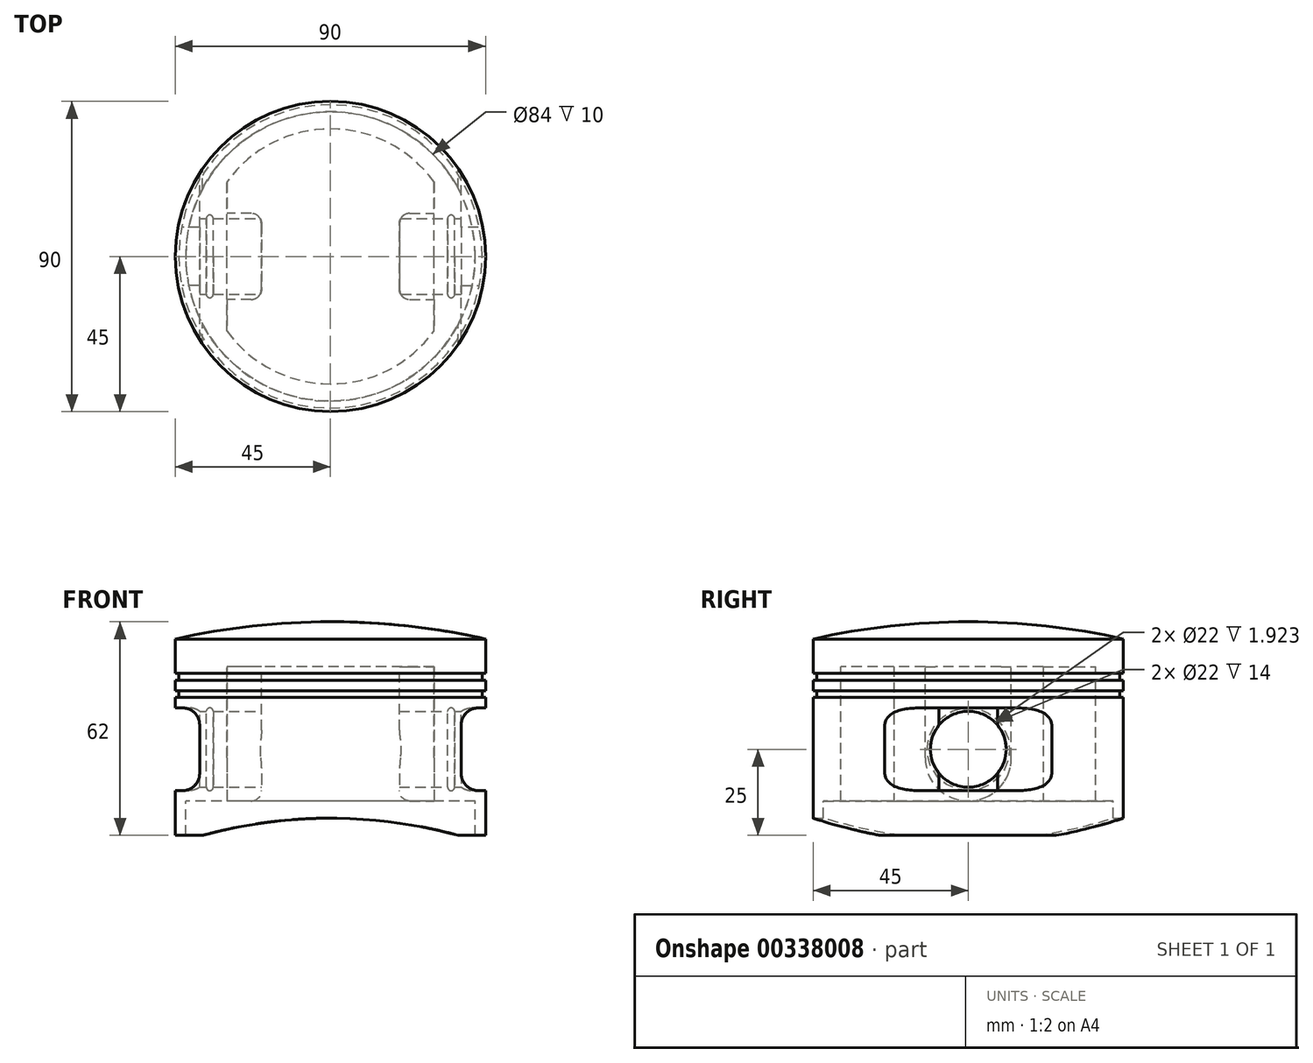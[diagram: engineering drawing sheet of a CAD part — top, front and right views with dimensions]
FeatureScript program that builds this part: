
annotation { "Feature Type Name" : "Feature", "Feature Type Description" : "" }
export const myFeature = defineFeature(function(context is Context, id is Id, definition is map)
    precondition{}
    {
        {
            var Q0;
            Q0=qCreatedBy(makeId("Front.planeOp"),FACE);
            var sketch = newSketch(context, id + "F0", { "sketchPlane" : qUnion([Q0])});
            skLineSegment(sketch, "E0", {"start": v(0, 31.06) * mm, "end": v(0, -35.72) * mm, "construction": true});
            skLineSegment(sketch, "E1", {"start": v(0, 0) * mm, "end": v(45, 0) * mm});
            skLineSegment(sketch, "E2", {"start": v(45, 0) * mm, "end": v(45, -10) * mm});
            skLineSegment(sketch, "E3", {"start": v(45, -10) * mm, "end": v(44, -10) * mm});
            skLineSegment(sketch, "E4", {"start": v(44, -10) * mm, "end": v(44, -12) * mm});
            skLineSegment(sketch, "E5", {"start": v(44, -12) * mm, "end": v(45, -12) * mm});
            skLineSegment(sketch, "E6", {"start": v(45, -12) * mm, "end": v(45, -15) * mm});
            skLineSegment(sketch, "E7", {"start": v(45, -15) * mm, "end": v(44, -15) * mm});
            skLineSegment(sketch, "E8", {"start": v(44, -15) * mm, "end": v(44, -17) * mm});
            skLineSegment(sketch, "E9", {"start": v(44, -17) * mm, "end": v(45, -17) * mm});
            skLineSegment(sketch, "E10", {"start": v(45, -17) * mm, "end": v(45, -57) * mm});
            skLineSegment(sketch, "E11", {"start": v(45, -57) * mm, "end": v(42, -57) * mm});
            skLineSegment(sketch, "E12", {"start": v(42, -57) * mm, "end": v(42, -47) * mm});
            skLineSegment(sketch, "E13", {"start": v(42, -47) * mm, "end": v(37, -47) * mm});
            skLineSegment(sketch, "E14", {"start": v(37, -47) * mm, "end": v(37, -8) * mm});
            skLineSegment(sketch, "E15", {"start": v(37, -8) * mm, "end": v(0, -8) * mm});
            skLineSegment(sketch, "E16", {"start": v(0, -8) * mm, "end": v(0, 0) * mm});
            skSolve(sketch);
        }
        {
            var Q0;
            Q0 = qSketchRegion(id + "F0", true);
            var Q1;
            Q1=sQuery(id+"F0.wireOp",EDGE,"E0");
            revolve(context, id + "F1", {"entities" : qUnion([Q0]), "axis" : qUnion([Q1]), "revolveType" : RevolveType.FULL});
        }
        {
            var Q0;
            Q0=qCreatedBy(makeId("Front.planeOp"),FACE);
            var sketch = newSketch(context, id + "F2", { "sketchPlane" : qUnion([Q0])});
            skLineSegment(sketch, "E17.bottom", {"start": v(51.92, -20) * mm, "end": v(37.92, -20) * mm});
            skLineSegment(sketch, "E17.top", {"start": v(51.92, -44) * mm, "end": v(37.92, -44) * mm});
            skLineSegment(sketch, "E17.left", {"start": v(51.92, -20) * mm, "end": v(51.92, -44) * mm});
            skLineSegment(sketch, "E17.right", {"start": v(37.92, -20) * mm, "end": v(37.92, -44) * mm});
            skPoint(sketch, "E17.middle", {"position": v(44.92, -32) * mm});
            skLineSegment(sketch, "E18.MirrorCS", {"start": v(-51.92, -20) * mm, "end": v(-37.92, -20) * mm});
            skLineSegment(sketch, "E19.MirrorCS", {"start": v(-37.92, -20) * mm, "end": v(-37.92, -44) * mm});
            skLineSegment(sketch, "E20.MirrorCS", {"start": v(-51.92, -44) * mm, "end": v(-37.92, -44) * mm});
            skLineSegment(sketch, "E21.MirrorCS", {"start": v(-51.92, -20) * mm, "end": v(-51.92, -44) * mm});
            skSolve(sketch);
        }
        {
            var Q0;
            Q0 = qSketchRegion(id + "F2", true);
            extrude(context, id + "F3", {"entities" : qUnion([Q0]), "operationType" : NewBodyOperationType.REMOVE, "depth" : 100 * mm, "symmetric" : true});
        }
        {
            var Q0;
            Q0=makeQuery(id+"F1.opRevolve","SWEPT_FACE",FACE,{"disambiguationData":[OSD([sQuery(id+"F0.wireOp",EDGE,"E13")])]});
            var sketch = newSketch(context, id + "F4", { "sketchPlane" : qUnion([Q0])});
            skLineSegment(sketch, "E22", {"start": v(0, 42) * mm, "end": v(0, -42) * mm, "construction": true});
            skLineSegment(sketch, "E23", {"start": v(30, 21.66) * mm, "end": v(30, -21.66) * mm});
            skLineSegment(sketch, "E24.MirrorCS", {"start": v(-30, 21.66) * mm, "end": v(-30, -21.66) * mm});
            skSolve(sketch);
        }
        {
            var Q0;
            {var subQ0=sQuery(id+"F4.wireOp",EDGE,"E24.MirrorCS");Q0=makeQuery(id+"F4.imprint","IMPRINT",FACE,{"disambiguationData":[TD([[makeQuery(id+"F4.imprint","IMPRINT",EDGE,{"derivedFrom":subQ0}),-1.0]])]});}
            var Q1;
            {var subQ0=sQuery(id+"F4.wireOp",EDGE,"E23");Q1=makeQuery(id+"F4.imprint","IMPRINT",FACE,{"disambiguationData":[TD([[makeQuery(id+"F4.imprint","IMPRINT",EDGE,{"derivedFrom":subQ0}),1.0]])]});}
            extrude(context, id + "F5", {"entities" : qUnion([Q0, Q1]), "operationType" : NewBodyOperationType.ADD, "endBound" : BoundingType.UP_TO_NEXT, "oppositeDirection" : true, "depth" : 25 * mm});
        }
        {
            var Q0;
            Q0=makeQuery(id+"F5.opExtrude","SWEPT_FACE",FACE,{"disambiguationData":[OSD([sQuery(id+"F4.wireOp",EDGE,"E24.MirrorCS")])]});
            var sketch = newSketch(context, id + "F6", { "sketchPlane" : qUnion([Q0])});
            skArc(sketch, "E25", {"start": v(-12.5, -34.5) * mm, "mid": v(0, -47) * mm, "end": v(12.5, -34.5) * mm});
            skPoint(sketch, "E25.centerSnap0", {"position": v(0, -47) * mm});
            skLineSegment(sketch, "E26", {"start": v(-12.5, -34.5) * mm, "end": v(-12.5, -8) * mm});
            skLineSegment(sketch, "E27.MirrorCS", {"start": v(12.5, -34.5) * mm, "end": v(12.5, -8) * mm});
            skLineSegment(sketch, "E28", {"start": v(-12.5, -8) * mm, "end": v(12.5, -8) * mm});
            skSolve(sketch);
        }
        {
            var Q0;
            Q0 = qSketchRegion(id + "F6", true);
            extrude(context, id + "F7", {"entities" : qUnion([Q0]), "depth" : 10 * mm});
        }
        {
            var Q0;
            Q0=makeQuery(id+"F7.opExtrude","SWEPT_BODY",BODY,{"disambiguationData":[OSD([sQuery(id+"F6.wireOp",EDGE,"E25"),sQuery(id+"F6.wireOp",EDGE,"E26"),sQuery(id+"F6.wireOp",EDGE,"E27.MirrorCS"),sQuery(id+"F6.wireOp",EDGE,"E28")])]});
            var Q1;
            Q1=qCreatedBy(makeId("Right.planeOp"),FACE);
            mirror(context, id + "F8", {"operationType" : NewBodyOperationType.ADD, "entities" : qUnion([Q0]), "mirrorPlane" : qUnion([Q1])});
        }
        {
            var Q0;
            Q0=makeQuery(id+"F3.boolean.opBoolean","COPY",FACE,{"derivedFrom":makeQuery(id+"F3.opExtrude","SWEPT_FACE",FACE,{"disambiguationData":[OSD([sQuery(id+"F2.wireOp",EDGE,"E17.right")])]})});
            var sketch = newSketch(context, id + "F9", { "sketchPlane" : qUnion([Q0])});
            skLineSegment(sketch, "E29", {"start": v(-24.22, -32) * mm, "end": v(24.22, -32) * mm, "construction": true});
            skCircle(sketch, "E30", {"center": v(0, -32) * mm, "radius": 11 * mm});
            skSolve(sketch);
        }
        {
            var Q0;
            Q0=makeQuery(id+"F9.imprint","IMPRINT",FACE,{"disambiguationData":[TD([[makeQuery(id+"F9.imprint","IMPRINT",EDGE,{"derivedFrom":sQuery(id+"F9.wireOp",EDGE,"E30")}),1.0]])]});
            extrude(context, id + "F10", {"entities" : qUnion([Q0]), "operationType" : NewBodyOperationType.REMOVE, "oppositeDirection" : true, "depth" : 100 * mm});
        }
        {
            var Q0;
            Q0=makeQuery(id+"F8.opPattern","COPY",EDGE,{"derivedFrom":makeQuery(id+"F7.opExtrude","CAP_EDGE",EDGE,{"disambiguationData":[OSD([sQuery(id+"F6.wireOp",EDGE,"E27.MirrorCS")])],"isStart":false}),"instanceName":"1"});
            var Q1;
            Q1=makeQuery(id+"F7.opExtrude","CAP_EDGE",EDGE,{"disambiguationData":[OSD([sQuery(id+"F6.wireOp",EDGE,"E26")])],"isStart":false});
            fillet(context, id + "F11", {"entities" : qUnion([Q0, Q1]), "radius" : 3 * mm, "tangentPropagation" : true, "allowEdgeOverflow" : false});
        }
        {
            var Q0;
            Q0=makeQuery(id+"F3.boolean.opBoolean","COPY",EDGE,{"derivedFrom":makeQuery(id+"F3.opExtrude","SWEPT_EDGE",EDGE,{"disambiguationData":[OSD([sQuery(id+"F2.wireOp",EDGE,"E18.MirrorCS"),sQuery(id+"F2.wireOp",EDGE,"E19.MirrorCS")])]})});
            var Q1;
            Q1=makeQuery(id+"F3.boolean.opBoolean","COPY",EDGE,{"derivedFrom":makeQuery(id+"F3.opExtrude","SWEPT_EDGE",EDGE,{"disambiguationData":[OSD([sQuery(id+"F2.wireOp",EDGE,"E19.MirrorCS"),sQuery(id+"F2.wireOp",EDGE,"E20.MirrorCS")])]})});
            var Q2;
            Q2=makeQuery(id+"F3.boolean.opBoolean","COPY",EDGE,{"derivedFrom":makeQuery(id+"F3.opExtrude","SWEPT_EDGE",EDGE,{"disambiguationData":[OSD([sQuery(id+"F2.wireOp",EDGE,"E17.bottom"),sQuery(id+"F2.wireOp",EDGE,"E17.right")])]})});
            var Q3;
            Q3=makeQuery(id+"F3.boolean.opBoolean","COPY",EDGE,{"derivedFrom":makeQuery(id+"F3.opExtrude","SWEPT_EDGE",EDGE,{"disambiguationData":[OSD([sQuery(id+"F2.wireOp",EDGE,"E17.top"),sQuery(id+"F2.wireOp",EDGE,"E17.right")])]})});
            fillet(context, id + "F12", {"entities" : qUnion([Q0, Q1, Q2, Q3]), "radius" : 5 * mm, "tangentPropagation" : true, "allowEdgeOverflow" : false});
        }
        {
            var Q0;
            Q0=qCreatedBy(makeId("Front.planeOp"),FACE);
            var sketch = newSketch(context, id + "F13", { "sketchPlane" : qUnion([Q0])});
            skPoint(sketch, "E31", {"position": v(-45, 0) * mm});
            skPoint(sketch, "E32", {"position": v(45, 0) * mm});
            skArc(sketch, "E33", {"start": v(45, 0) * mm, "mid": v(22.64, 3.75) * mm, "end": v(0, 5) * mm});
            skLineSegment(sketch, "E34", {"start": v(0, 0) * mm, "end": v(45, 0) * mm});
            skLineSegment(sketch, "E35", {"start": v(0, 5) * mm, "end": v(0, 0) * mm});
            skSolve(sketch);
        }
        {
            var Q0;
            Q0 = qSketchRegion(id + "F13", true);
            var Q1;
            Q1=sQuery(id+"F0.wireOp",EDGE,"E0");
            revolve(context, id + "F14", {"operationType" : NewBodyOperationType.ADD, "entities" : qUnion([Q0]), "axis" : qUnion([Q1]), "revolveType" : RevolveType.FULL});
        }
        {
            var Q0;
            Q0=qCreatedBy(makeId("Front.planeOp"),FACE);
            var sketch = newSketch(context, id + "F15", { "sketchPlane" : qUnion([Q0])});
            skLineSegment(sketch, "E36", {"start": v(0, -57) * mm, "end": v(0, -192) * mm, "construction": true});
            skCircle(sketch, "E37", {"center": v(0, -192) * mm, "radius": 140 * mm});
            skSolve(sketch);
        }
        {
            var Q0;
            Q0 = qSketchRegion(id + "F15", true);
            extrude(context, id + "F16", {"entities" : qUnion([Q0]), "operationType" : NewBodyOperationType.REMOVE, "depth" : 100 * mm, "symmetric" : true});
        }
        {
            var Q0;
            Q0=qCreatedBy(makeId("Front.planeOp"),FACE);
            var sketch = newSketch(context, id + "F17", { "sketchPlane" : qUnion([Q0])});
            skCircle(sketch, "E38", {"center": v(-35, -21) * mm, "radius": 1 * mm});
            skPoint(sketch, "E39", {"position": v(-45, -57) * mm});
            skCircle(sketch, "E40.MirrorC", {"center": v(35, -21) * mm, "radius": 1 * mm});
            skLineSegment(sketch, "E41", {"start": v(-37.92, -32) * mm, "end": v(37.92, -32) * mm, "construction": true});
            skSolve(sketch);
        }
        {
            var Q0;
            Q0 = qSketchRegion(id + "F17", true);
            var Q1;
            Q1=sQuery(id+"F17.wireOp",EDGE,"E41");
            revolve(context, id + "F18", {"operationType" : NewBodyOperationType.REMOVE, "entities" : qUnion([Q0]), "axis" : qUnion([Q1]), "revolveType" : RevolveType.FULL, "oppositeDirection" : true});
        }
    });
